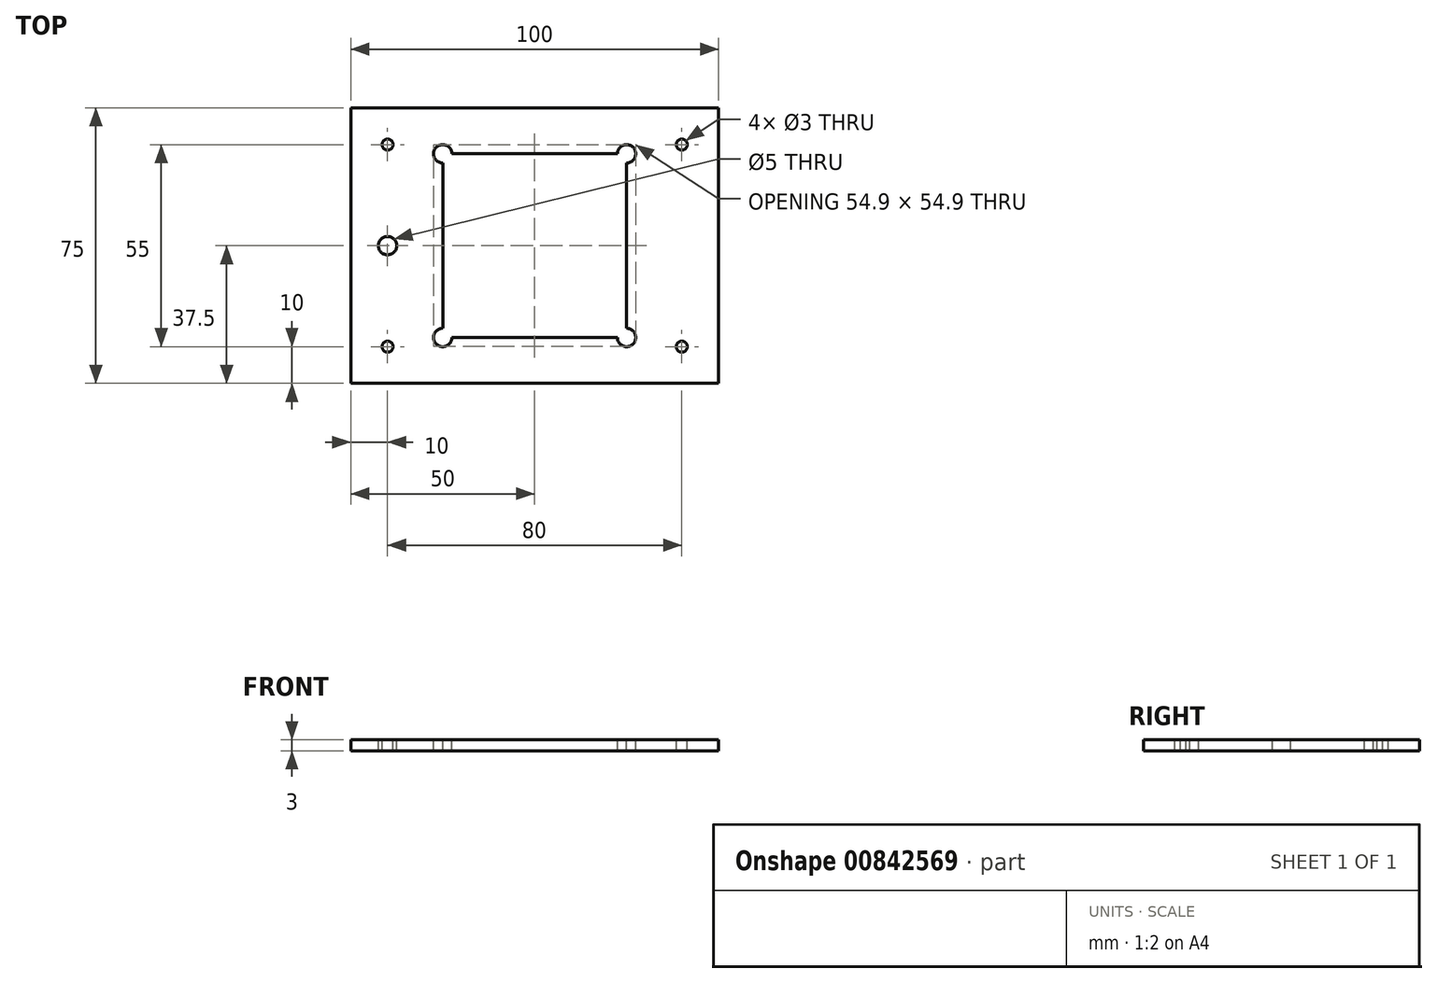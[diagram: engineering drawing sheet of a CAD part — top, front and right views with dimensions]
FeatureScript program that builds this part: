
annotation { "Feature Type Name" : "Feature", "Feature Type Description" : "" }
export const myFeature = defineFeature(function(context is Context, id is Id, definition is map)
    precondition{}
    {
        {
            var Q0;
            Q0=qCreatedBy(makeId("Top.planeOp"),FACE);
            var sketch = newSketch(context, id + "F0", { "sketchPlane" : qUnion([Q0])});
            skLineSegment(sketch, "E0.bottom", {"start": v(0, 0) * mm, "end": v(100, 0) * mm});
            skLineSegment(sketch, "E0.top", {"start": v(0, 75) * mm, "end": v(100, 75) * mm});
            skLineSegment(sketch, "E0.left", {"start": v(0, 0) * mm, "end": v(0, 75) * mm});
            skLineSegment(sketch, "E0.right", {"start": v(100, 0) * mm, "end": v(100, 75) * mm});
            skCircle(sketch, "E1", {"center": v(10, 65) * mm, "radius": 1.5 * mm});
            skCircle(sketch, "E2", {"center": v(10, 10) * mm, "radius": 1.5 * mm});
            skCircle(sketch, "E3", {"center": v(90, 10) * mm, "radius": 1.5 * mm});
            skCircle(sketch, "E4", {"center": v(90, 65) * mm, "radius": 1.5 * mm});
            skCircle(sketch, "E5", {"center": v(10, 37.5) * mm, "radius": 2.5 * mm});
            skLineSegment(sketch, "E6.bottom", {"start": v(75, 62.5) * mm, "end": v(25, 62.5) * mm});
            skLineSegment(sketch, "E6.top", {"start": v(75, 12.5) * mm, "end": v(25, 12.5) * mm});
            skLineSegment(sketch, "E6.left", {"start": v(75, 62.5) * mm, "end": v(75, 12.5) * mm});
            skLineSegment(sketch, "E6.right", {"start": v(25, 62.5) * mm, "end": v(25, 12.5) * mm});
            skPoint(sketch, "E6.middle", {"position": v(50, 37.5) * mm});
            skArc(sketch, "E7", {"start": v(25, 60) * mm, "mid": v(23.23, 64.27) * mm, "end": v(27.5, 62.5) * mm});
            skArc(sketch, "E8", {"start": v(72.5, 62.5) * mm, "mid": v(76.77, 64.27) * mm, "end": v(75, 60) * mm});
            skArc(sketch, "E9", {"start": v(75, 15) * mm, "mid": v(76.77, 10.73) * mm, "end": v(72.5, 12.5) * mm});
            skArc(sketch, "E10", {"start": v(27.5, 12.5) * mm, "mid": v(23.23, 10.73) * mm, "end": v(25, 15) * mm});
            skSolve(sketch);
        }
        {
            var Q0;
            Q0=makeQuery(id+"F0.imprint","IMPRINT",FACE,{"disambiguationData":[TD([[makeQuery(id+"F0.imprint","IMPRINT",EDGE,{"derivedFrom":sQuery(id+"F0.wireOp",EDGE,"E0.bottom")}),1.0]])]});
            extrude(context, id + "F1", {"entities" : qUnion([Q0]), "oppositeDirection" : true, "depth" : 3 * mm, "offsetDistance" : 25 * mm});
        }
    });
